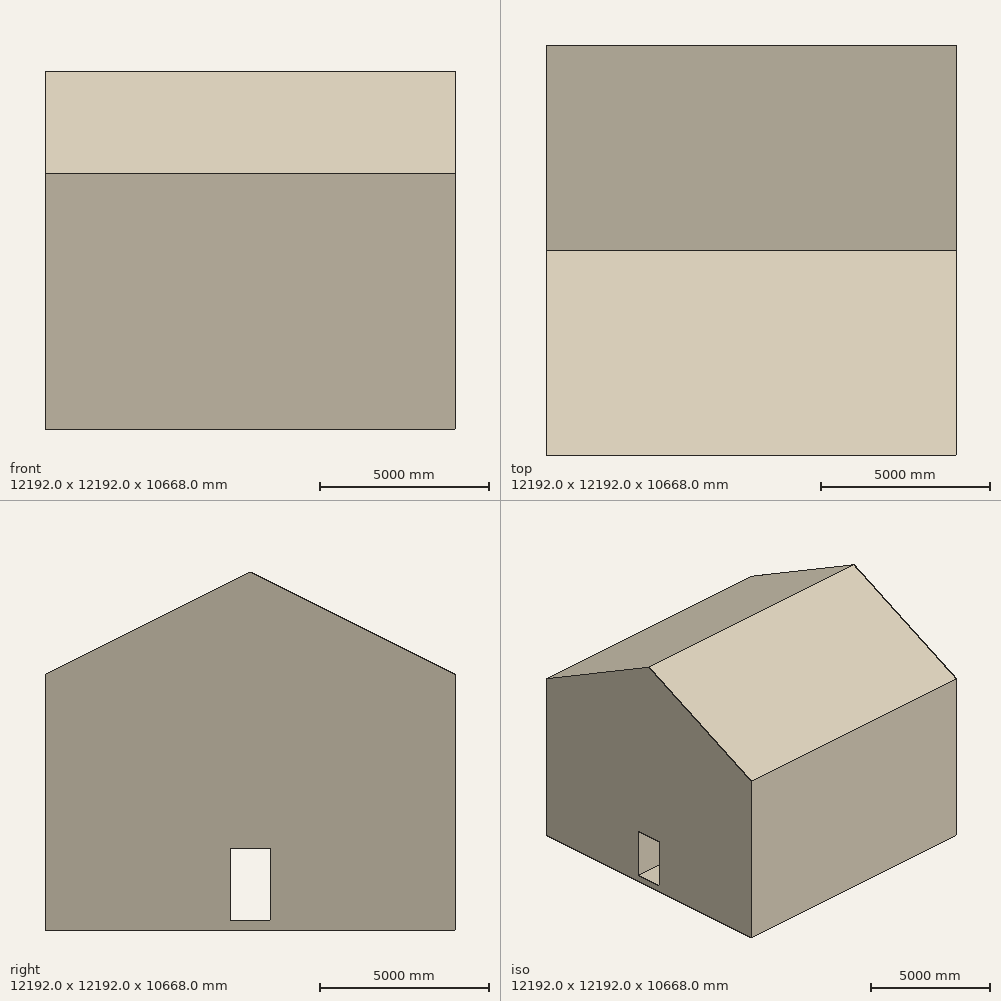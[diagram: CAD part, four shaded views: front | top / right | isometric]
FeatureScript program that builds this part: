
annotation { "Feature Type Name" : "Feature", "Feature Type Description" : "" }
export const myFeature = defineFeature(function(context is Context, id is Id, definition is map)
    precondition{}
    {
        {
            var Q0;
            Q0=qCreatedBy(makeId("Right.planeOp"),FACE);
            var sketch = newSketch(context, id + "F0", { "sketchPlane" : qUnion([Q0])});
            skLineSegment(sketch, "E0", {"start": v(0, 0) * mm, "end": v(-6096, 0) * mm});
            skLineSegment(sketch, "E1", {"start": v(-6096, 0) * mm, "end": v(-12192, 0) * mm});
            skLineSegment(sketch, "E2", {"start": v(-12192, 0) * mm, "end": v(-6096, 3048) * mm});
            skLineSegment(sketch, "E3", {"start": v(-6096, 3048) * mm, "end": v(0, 0) * mm});
            skLineSegment(sketch, "E4", {"start": v(-12192, 0) * mm, "end": v(-12192, -7315.2) * mm});
            skLineSegment(sketch, "E5", {"start": v(-12192, -7315.2) * mm, "end": v(0, -7315.2) * mm});
            skLineSegment(sketch, "E6", {"start": v(0, 0) * mm, "end": v(0, -7315.2) * mm});
            skLineSegment(sketch, "E7", {"start": v(-12192, -7620) * mm, "end": v(0, -7620) * mm});
            skLineSegment(sketch, "E8", {"start": v(-12192, -7315.2) * mm, "end": v(-12192, -7620) * mm});
            skLineSegment(sketch, "E9", {"start": v(0, -7315.2) * mm, "end": v(0, -7620) * mm});
            skLineSegment(sketch, "E10", {"start": v(-6096, -7315.2) * mm, "end": v(-6705.6, -7315.2) * mm});
            skLineSegment(sketch, "E11", {"start": v(-6705.6, -7315.2) * mm, "end": v(-6705.6, -5181.6) * mm});
            skLineSegment(sketch, "E12", {"start": v(-6705.6, -5181.6) * mm, "end": v(-6096, -5181.6) * mm});
            skLineSegment(sketch, "E13", {"start": v(-6096, -5181.6) * mm, "end": v(-5486.4, -5181.6) * mm});
            skLineSegment(sketch, "E14", {"start": v(-5486.4, -5181.6) * mm, "end": v(-5486.4, -7315.2) * mm});
            skLineSegment(sketch, "E15", {"start": v(-5486.4, -7315.2) * mm, "end": v(-6096, -7315.2) * mm});
            skLineSegment(sketch, "E16.bottom", {"start": v(-11277.6, -914.4) * mm, "end": v(-9448.8, -914.4) * mm});
            skLineSegment(sketch, "E16.top", {"start": v(-11277.6, -2133.6) * mm, "end": v(-9448.8, -2133.6) * mm});
            skLineSegment(sketch, "E16.left", {"start": v(-11277.6, -914.4) * mm, "end": v(-11277.6, -2133.6) * mm});
            skLineSegment(sketch, "E16.right", {"start": v(-9448.8, -914.4) * mm, "end": v(-9448.8, -2133.6) * mm});
            skLineSegment(sketch, "E17.bottom", {"start": v(-3048, -914.4) * mm, "end": v(-1524, -914.4) * mm});
            skLineSegment(sketch, "E17.top", {"start": v(-3048, -2743.2) * mm, "end": v(-1524, -2743.2) * mm});
            skLineSegment(sketch, "E17.left", {"start": v(-3048, -914.4) * mm, "end": v(-3048, -2743.2) * mm});
            skLineSegment(sketch, "E17.right", {"start": v(-1524, -914.4) * mm, "end": v(-1524, -2743.2) * mm});
            skLineSegment(sketch, "E18.0", {"start": v(-3352.8, -609.6) * mm, "end": v(-3352.8, -3048) * mm});
            skLineSegment(sketch, "E18.1", {"start": v(-3352.8, -609.6) * mm, "end": v(-1219.2, -609.6) * mm});
            skLineSegment(sketch, "E18.2", {"start": v(-1219.2, -609.6) * mm, "end": v(-1219.2, -3048) * mm});
            skLineSegment(sketch, "E18.3", {"start": v(-3352.8, -3048) * mm, "end": v(-1219.2, -3048) * mm});
            skLineSegment(sketch, "E19.0", {"start": v(-11582.4, -609.6) * mm, "end": v(-9144, -609.6) * mm});
            skLineSegment(sketch, "E19.1", {"start": v(-11582.4, -609.6) * mm, "end": v(-11582.4, -2438.4) * mm});
            skLineSegment(sketch, "E19.2", {"start": v(-11582.4, -2438.4) * mm, "end": v(-9144, -2438.4) * mm});
            skLineSegment(sketch, "E19.3", {"start": v(-9144, -609.6) * mm, "end": v(-9144, -2438.4) * mm});
            skLineSegment(sketch, "E20.bottom", {"start": v(-10363.2, -4876.8) * mm, "end": v(-8839.2, -4876.8) * mm});
            skLineSegment(sketch, "E20.top", {"start": v(-10363.2, -6400.8) * mm, "end": v(-8839.2, -6400.8) * mm});
            skLineSegment(sketch, "E20.left", {"start": v(-10363.2, -4876.8) * mm, "end": v(-10363.2, -6400.8) * mm});
            skLineSegment(sketch, "E20.right", {"start": v(-8839.2, -4876.8) * mm, "end": v(-8839.2, -6400.8) * mm});
            skLineSegment(sketch, "E21.0", {"start": v(-10668, -4572) * mm, "end": v(-8534.4, -4572) * mm});
            skLineSegment(sketch, "E21.1", {"start": v(-10668, -4572) * mm, "end": v(-10668, -6705.6) * mm});
            skLineSegment(sketch, "E21.2", {"start": v(-10668, -6705.6) * mm, "end": v(-8534.4, -6705.6) * mm});
            skLineSegment(sketch, "E21.3", {"start": v(-8534.4, -4572) * mm, "end": v(-8534.4, -6705.6) * mm});
            skLineSegment(sketch, "E22.bottom", {"start": v(-3048, -5181.6) * mm, "end": v(-1219.2, -5181.6) * mm});
            skLineSegment(sketch, "E22.top", {"start": v(-3048, -7010.4) * mm, "end": v(-1219.2, -7010.4) * mm});
            skLineSegment(sketch, "E22.left", {"start": v(-3048, -5181.6) * mm, "end": v(-3048, -7010.4) * mm});
            skLineSegment(sketch, "E22.right", {"start": v(-1219.2, -5181.6) * mm, "end": v(-1219.2, -7010.4) * mm});
            skLineSegment(sketch, "E23.0", {"start": v(-3352.8, -4876.8) * mm, "end": v(-914.4, -4876.8) * mm});
            skLineSegment(sketch, "E23.1", {"start": v(-3352.8, -4876.8) * mm, "end": v(-3352.8, -7315.2) * mm});
            skLineSegment(sketch, "E23.2", {"start": v(-3352.8, -7315.2) * mm, "end": v(-914.4, -7315.2) * mm});
            skLineSegment(sketch, "E23.3", {"start": v(-914.4, -4876.8) * mm, "end": v(-914.4, -7315.2) * mm});
            skSolve(sketch);
        }
        {
            var Q0;
            Q0=makeQuery(id+"F0.imprint","IMPRINT",FACE,{"disambiguationData":[TD([[makeQuery(id+"F0.imprint","IMPRINT",EDGE,{"derivedFrom":sQuery(id+"F0.wireOp",EDGE,"E7")}),1.0]])]});
            var Q1;
            Q1=makeQuery(id+"F0.imprint","IMPRINT",FACE,{"disambiguationData":[TD([[makeQuery(id+"F0.imprint","IMPRINT",EDGE,{"derivedFrom":sQuery(id+"F0.wireOp",EDGE,"E0")}),1.0]])]});
            var Q2;
            Q2=makeQuery(id+"F0.imprint","IMPRINT",FACE,{"disambiguationData":[TD([[makeQuery(id+"F0.imprint","IMPRINT",EDGE,{"derivedFrom":sQuery(id+"F0.wireOp",EDGE,"E17.bottom")}),-1.0]])]});
            var Q3;
            Q3=makeQuery(id+"F0.imprint","IMPRINT",FACE,{"disambiguationData":[TD([[makeQuery(id+"F0.imprint","IMPRINT",EDGE,{"derivedFrom":sQuery(id+"F0.wireOp",EDGE,"E22.bottom")}),-1.0]])]});
            var Q4;
            Q4=makeQuery(id+"F0.imprint","IMPRINT",FACE,{"disambiguationData":[TD([[makeQuery(id+"F0.imprint","IMPRINT",EDGE,{"derivedFrom":sQuery(id+"F0.wireOp",EDGE,"E20.bottom")}),1.0]])]});
            var Q5;
            Q5=makeQuery(id+"F0.imprint","IMPRINT",FACE,{"disambiguationData":[TD([[makeQuery(id+"F0.imprint","IMPRINT",EDGE,{"derivedFrom":sQuery(id+"F0.wireOp",EDGE,"E22.bottom")}),1.0]])]});
            var Q6;
            Q6=makeQuery(id+"F0.imprint","IMPRINT",FACE,{"disambiguationData":[TD([[makeQuery(id+"F0.imprint","IMPRINT",EDGE,{"derivedFrom":sQuery(id+"F0.wireOp",EDGE,"E10")}),-1.0]])]});
            var Q7;
            Q7=makeQuery(id+"F0.imprint","IMPRINT",FACE,{"disambiguationData":[TD([[makeQuery(id+"F0.imprint","IMPRINT",EDGE,{"derivedFrom":sQuery(id+"F0.wireOp",EDGE,"E16.bottom")}),1.0]])]});
            var Q8;
            Q8=makeQuery(id+"F0.imprint","IMPRINT",FACE,{"disambiguationData":[TD([[makeQuery(id+"F0.imprint","IMPRINT",EDGE,{"derivedFrom":sQuery(id+"F0.wireOp",EDGE,"E17.bottom")}),1.0]])]});
            var Q9;
            Q9=makeQuery(id+"F0.imprint","IMPRINT",FACE,{"disambiguationData":[TD([[makeQuery(id+"F0.imprint","IMPRINT",EDGE,{"derivedFrom":sQuery(id+"F0.wireOp",EDGE,"E20.bottom")}),-1.0]])]});
            var Q10;
            Q10=makeQuery(id+"F0.imprint","IMPRINT",FACE,{"disambiguationData":[TD([[makeQuery(id+"F0.imprint","IMPRINT",EDGE,{"derivedFrom":sQuery(id+"F0.wireOp",EDGE,"E0")}),-1.0]])]});
            var Q11;
            Q11=makeQuery(id+"F0.imprint","IMPRINT",FACE,{"disambiguationData":[TD([[makeQuery(id+"F0.imprint","IMPRINT",EDGE,{"derivedFrom":sQuery(id+"F0.wireOp",EDGE,"E16.bottom")}),-1.0]])]});
            extrude(context, id + "F1", {"entities" : qUnion([Q0, Q1, Q2, Q3, Q4, Q5, Q6, Q7, Q8, Q9, Q10, Q11]), "depth" : 12192 * mm, "offsetDistance" : 30.48 * mm});
        }
        {
            var Q0;
            Q0=makeQuery(id+"F0.imprint","IMPRINT",FACE,{"disambiguationData":[TD([[makeQuery(id+"F0.imprint","IMPRINT",EDGE,{"derivedFrom":sQuery(id+"F0.wireOp",EDGE,"E0")}),-1.0]])]});
            var Q1;
            Q1=makeQuery(id+"F0.imprint","IMPRINT",FACE,{"disambiguationData":[TD([[makeQuery(id+"F0.imprint","IMPRINT",EDGE,{"derivedFrom":sQuery(id+"F0.wireOp",EDGE,"E0")}),1.0]])]});
            extrude(context, id + "F2", {"entities" : qUnion([Q0, Q1]), "operationType" : NewBodyOperationType.ADD, "depth" : 30.48 * mm, "offsetDistance" : 30.48 * mm});
        }
    });
